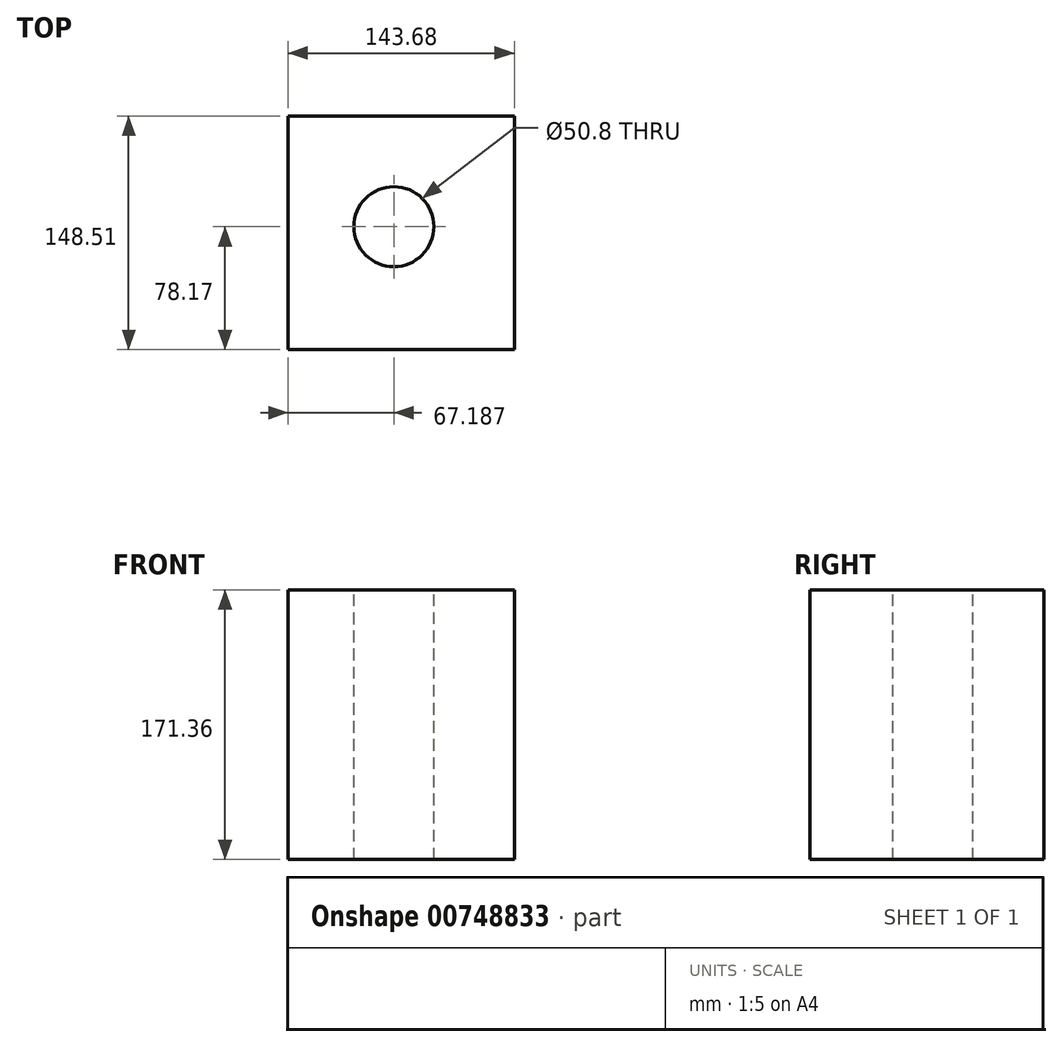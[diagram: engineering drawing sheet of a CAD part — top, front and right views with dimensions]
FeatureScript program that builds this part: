
annotation { "Feature Type Name" : "Feature", "Feature Type Description" : "" }
export const myFeature = defineFeature(function(context is Context, id is Id, definition is map)
    precondition{}
    {
        {
            var Q0;
            Q0=qCreatedBy(makeId("Top.planeOp"),FACE);
            var sketch = newSketch(context, id + "F0", { "sketchPlane" : qUnion([Q0])});
            skLineSegment(sketch, "E0.bottom", {"start": v(-31.87, 7.3) * mm, "end": v(111.81, 7.3) * mm});
            skLineSegment(sketch, "E0.top", {"start": v(-31.87, 155.8) * mm, "end": v(111.81, 155.8) * mm});
            skLineSegment(sketch, "E0.left", {"start": v(-31.87, 7.3) * mm, "end": v(-31.87, 155.8) * mm});
            skLineSegment(sketch, "E0.right", {"start": v(111.81, 7.3) * mm, "end": v(111.81, 155.8) * mm});
            skSolve(sketch);
        }
        {
            var Q0;
            Q0 = qSketchRegion(id + "F0", true);
            extrude(context, id + "F1", {"entities" : qUnion([Q0]), "depth" : 171.36 * mm, "offsetDistance" : 25.4 * mm});
        }
        {
            var Q0;
            Q0=makeQuery(id+"F1.opExtrude","CAP_FACE",FACE,{"disambiguationData":[OSD([sQuery(id+"F0.wireOp",EDGE,"E0.bottom"),sQuery(id+"F0.wireOp",EDGE,"E0.top"),sQuery(id+"F0.wireOp",EDGE,"E0.left"),sQuery(id+"F0.wireOp",EDGE,"E0.right")])],"isStart":false});
            var sketch = newSketch(context, id + "F2", { "sketchPlane" : qUnion([Q0])});
            skCircle(sketch, "E1", {"center": v(35.32, 85.47) * mm, "radius": 42.3 * mm});
            skSolve(sketch);
        }
        {
            var Q0;
            Q0=sQuery(id+"F2.wireOp",VERTEX,"E1.center");
            var Q1;
            Q1=makeQuery(id+"F1.opExtrude","SWEPT_BODY",BODY,{"disambiguationData":[OSD([sQuery(id+"F0.wireOp",EDGE,"E0.bottom"),sQuery(id+"F0.wireOp",EDGE,"E0.top"),sQuery(id+"F0.wireOp",EDGE,"E0.left"),sQuery(id+"F0.wireOp",EDGE,"E0.right")])]});
            hole(context, id + "F3", {"style" : HoleStyle.SIMPLE, "endStyle" : HoleEndStyle.THROUGH, "holeDiameter" : 50.8 * mm, "majorDiameter" : 6.35 * mm, "isTappedThrough" : true, "tappedDepth" : 12.7 * mm, "tapClearance" : 3, "locations" : qUnion([Q0]), "scope" : qUnion([Q1])});
        }
    });
